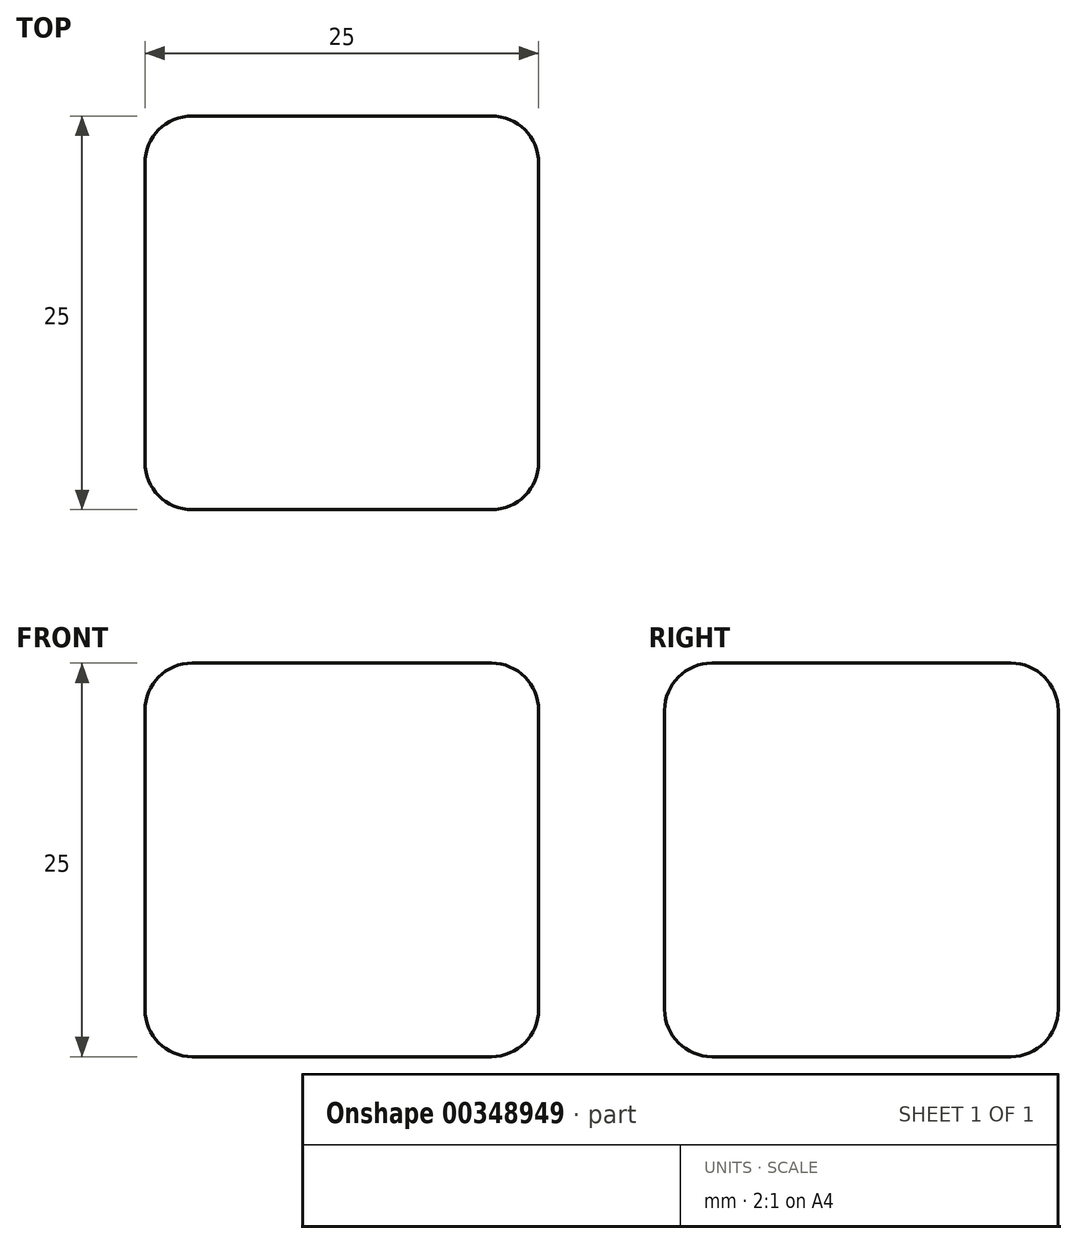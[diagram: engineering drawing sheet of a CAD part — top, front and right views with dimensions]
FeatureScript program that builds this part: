
annotation { "Feature Type Name" : "Feature", "Feature Type Description" : "" }
export const myFeature = defineFeature(function(context is Context, id is Id, definition is map)
    precondition{}
    {
        {
            var Q0;
            Q0=qCreatedBy(makeId("Front.planeOp"),FACE);
            var sketch = newSketch(context, id + "F0", { "sketchPlane" : qUnion([Q0])});
            skLineSegment(sketch, "E0.bottom", {"start": v(0, 0) * mm, "end": v(-25, 0) * mm});
            skLineSegment(sketch, "E0.top", {"start": v(0, 25) * mm, "end": v(-25, 25) * mm});
            skLineSegment(sketch, "E0.left", {"start": v(0, 0) * mm, "end": v(0, 25) * mm});
            skLineSegment(sketch, "E0.right", {"start": v(-25, 0) * mm, "end": v(-25, 25) * mm});
            skSolve(sketch);
        }
        {
            var Q0;
            Q0=makeQuery(id+"F0.imprint","IMPRINT",FACE,{"disambiguationData":[TD([[makeQuery(id+"F0.imprint","IMPRINT",EDGE,{"derivedFrom":sQuery(id+"F0.wireOp",EDGE,"E0.bottom")}),-1.0]])]});
            extrude(context, id + "F1", {"entities" : qUnion([Q0]), "depth" : 25 * mm});
        }
        {
            var Q0;
            Q0=makeQuery(id+"F1.opExtrude","SWEPT_EDGE",EDGE,{"disambiguationData":[OSD([sQuery(id+"F0.wireOp",EDGE,"E0.bottom"),sQuery(id+"F0.wireOp",EDGE,"E0.left")])]});
            fillet(context, id + "F2", {"entities" : qUnion([Q0]), "radius" : 3 * mm, "tangentPropagation" : true, "allowEdgeOverflow" : false});
        }
        {
            var Q0;
            Q0=makeQuery(id+"F1.opExtrude","SWEPT_EDGE",EDGE,{"disambiguationData":[OSD([sQuery(id+"F0.wireOp",EDGE,"E0.bottom"),sQuery(id+"F0.wireOp",EDGE,"E0.right")])]});
            var Q1;
            Q1=makeQuery(id+"F1.opExtrude","CAP_EDGE",EDGE,{"disambiguationData":[OSD([sQuery(id+"F0.wireOp",EDGE,"E0.bottom")])],"isStart":false});
            var Q2;
            Q2=makeQuery(id+"F1.opExtrude","CAP_EDGE",EDGE,{"disambiguationData":[OSD([sQuery(id+"F0.wireOp",EDGE,"E0.right")])],"isStart":false});
            fillet(context, id + "F3", {"entities" : qUnion([Q0, Q1, Q2]), "radius" : 3 * mm, "tangentPropagation" : true, "allowEdgeOverflow" : false});
        }
        {
            var Q0;
            Q0=makeQuery(id+"F1.opExtrude","CAP_EDGE",EDGE,{"disambiguationData":[OSD([sQuery(id+"F0.wireOp",EDGE,"E0.bottom")])],"isStart":true});
            var Q1;
            Q1=makeQuery(id+"F1.opExtrude","CAP_EDGE",EDGE,{"disambiguationData":[OSD([sQuery(id+"F0.wireOp",EDGE,"E0.left")])],"isStart":true});
            var Q2;
            Q2=makeQuery(id+"F1.opExtrude","CAP_EDGE",EDGE,{"disambiguationData":[OSD([sQuery(id+"F0.wireOp",EDGE,"E0.right")])],"isStart":true});
            var Q3;
            Q3=makeQuery(id+"F1.opExtrude","CAP_EDGE",EDGE,{"disambiguationData":[OSD([sQuery(id+"F0.wireOp",EDGE,"E0.top")])],"isStart":true});
            fillet(context, id + "F4", {"entities" : qUnion([Q0, Q1, Q2, Q3]), "radius" : 3 * mm, "tangentPropagation" : true, "allowEdgeOverflow" : false});
        }
        {
            var Q0;
            Q0=makeQuery(id+"F1.opExtrude","SWEPT_EDGE",EDGE,{"disambiguationData":[OSD([sQuery(id+"F0.wireOp",EDGE,"E0.top"),sQuery(id+"F0.wireOp",EDGE,"E0.right")])]});
            var Q1;
            Q1=makeQuery(id+"F1.opExtrude","CAP_EDGE",EDGE,{"disambiguationData":[OSD([sQuery(id+"F0.wireOp",EDGE,"E0.top")])],"isStart":false});
            var Q2;
            Q2=makeQuery(id+"F1.opExtrude","SWEPT_EDGE",EDGE,{"disambiguationData":[OSD([sQuery(id+"F0.wireOp",EDGE,"E0.top"),sQuery(id+"F0.wireOp",EDGE,"E0.left")])]});
            fillet(context, id + "F5", {"entities" : qUnion([Q0, Q1, Q2]), "radius" : 3 * mm, "tangentPropagation" : true, "allowEdgeOverflow" : false});
        }
    });
